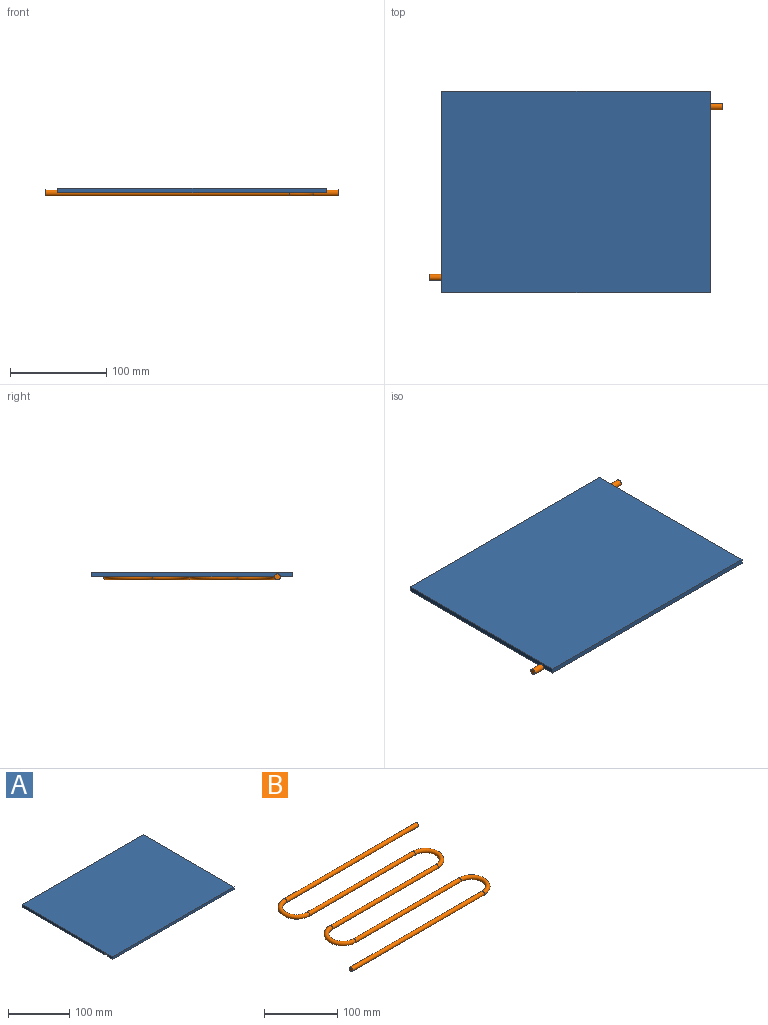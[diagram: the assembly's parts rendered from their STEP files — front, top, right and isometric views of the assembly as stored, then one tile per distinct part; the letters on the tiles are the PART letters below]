
ASSEMBLY  parts=2 mates=1
PART A: 16 faces, bbox 279.4x209.6x7.3 mm
  f0: plane 209.55x5.08mm, normal (-1,0,0), area 1048.7mm2, adj f2,f3,f4,f5,f6,f7
  f1: plane 209.55x5.08mm, normal (1,0,0), area 1048.7mm2, adj f2,f3,f4,f5,f6,f15
  f2: plane 279.4x190.5mm, normal (0,0,-1), area 24919.7mm2, adj f0,f1,f3,f7,f8,f9,f10,f11
  f3: plane 279.4x5.08mm, normal (0,-1,0), area 1419.4mm2, adj f0,f1,f2,f5
  f4: plane 279.4x5.08mm, normal (0,1,0), area 1419.4mm2, adj f0,f1,f5,f6
  f5: plane 279.4x209.55mm, normal (0,0,1), area 58548.3mm2, adj f0,f1,f3,f4
  f6: plane 279.4x190.5mm, normal (0,0,-1), area 24919.7mm2, adj f0,f1,f4,f7,f8,f9,f10,f11
  f7: cylinder r=3.17mm len=241.3mm, axis (1,0,0), area 2406.9mm2, adj f0,f2,f6,f8
  f8: torus R=22.23mm, axis (0,0,1), area 696.4mm2, adj f2,f6,f7,f9
  f9: cylinder r=3.17mm len=203.2mm, axis (-1,0,0), area 2026.8mm2, adj f2,f6,f8,f10
  f10: torus R=22.23mm, axis (0,0,-1), area 696.4mm2, adj f2,f6,f9,f11
  f11: cylinder r=3.17mm len=203.2mm, axis (1,0,0), area 2026.8mm2, adj f2,f6,f10,f12
  f12: torus R=22.23mm, axis (0,0,1), area 696.4mm2, adj f2,f6,f11,f13
  f13: cylinder r=3.17mm len=203.2mm, axis (-1,0,0), area 2026.8mm2, adj f2,f6,f12,f14
  f14: torus R=22.23mm, axis (0,0,-1), area 696.4mm2, adj f2,f6,f13,f15
  f15: cylinder r=3.17mm len=241.3mm, axis (1,0,0), area 2406.9mm2, adj f1,f2,f6,f14
PART B: 11 faces, bbox 304.8x188.3x6.4 mm
  f0: plane 6.35x6.35mm, normal (-1,0,0), area 31.7mm2, adj f2
  f1: plane 6.35x6.35mm, normal (1,0,0), area 31.7mm2, adj f10
  f2: cylinder r=3.17mm len=254mm, axis (1,0,0), area 5067.1mm2, adj f0,f3
  f3: torus R=22.23mm, axis (0,0,1), area 1392.9mm2, adj f2,f4
  f4: cylinder r=3.17mm len=203.2mm, axis (-1,0,0), area 4053.7mm2, adj f3,f5
  f5: torus R=22.23mm, axis (0,0,-1), area 1392.9mm2, adj f4,f6
  f6: cylinder r=3.17mm len=203.2mm, axis (1,0,0), area 4053.7mm2, adj f5,f7
  f7: torus R=22.23mm, axis (0,0,1), area 1392.9mm2, adj f6,f8
  f8: cylinder r=3.17mm len=203.2mm, axis (-1,0,0), area 4053.7mm2, adj f7,f9
  f9: torus R=22.23mm, axis (0,0,-1), area 1392.9mm2, adj f8,f10
  f10: cylinder r=3.17mm len=254mm, axis (1,0,0), area 5067.1mm2, adj f1,f9
PLACE A t=(-21.19,-17.59,31.84)mm
PLACE B rot(axis=(0,0,1),180deg) t=(105.81,79.56,31.84)mm
MATE fastened B.f2 <-> A.f15  axis (1,0,0) through (258.21,176.09,31.84)mm
